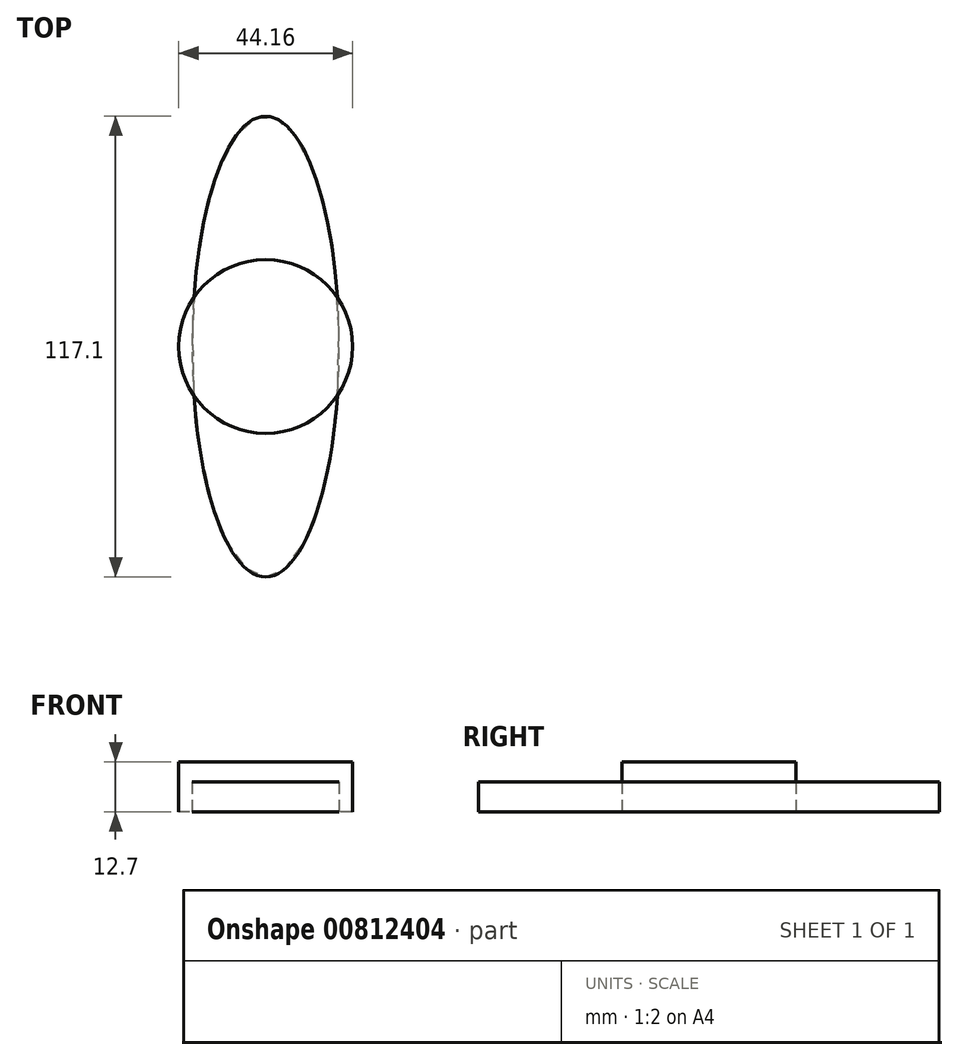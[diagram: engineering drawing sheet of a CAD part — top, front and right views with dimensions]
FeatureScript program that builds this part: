
annotation { "Feature Type Name" : "Feature", "Feature Type Description" : "" }
export const myFeature = defineFeature(function(context is Context, id is Id, definition is map)
    precondition{}
    {
        {
            var Q0;
            Q0=qCreatedBy(makeId("Top.planeOp"),FACE);
            var sketch = newSketch(context, id + "F0", { "sketchPlane" : qUnion([Q0])});
            skCircle(sketch, "E0", {"center": v(0, 0) * mm, "radius": 22.08 * mm});
            skSolve(sketch);
        }
        {
            var Q0;
            Q0 = qSketchRegion(id + "F0", true);
            extrude(context, id + "F1", {"entities" : qUnion([Q0]), "depth" : 12.7 * mm, "offsetDistance" : 25.4 * mm});
        }
        {
            var Q0;
            Q0=qCreatedBy(makeId("Top.planeOp"),FACE);
            var sketch = newSketch(context, id + "F2", { "sketchPlane" : qUnion([Q0])});
            skEllipse(sketch, "E1", {"center": v(0, 0) * mm, "majorRadius": 59.16 * mm, "minorRadius": 17.85 * mm, "majorAxis": v(1, 0)});
            skSolve(sketch);
        }
        {
            var Q0;
            Q0=makeQuery(id+"F2.imprint","IMPRINT",FACE,{"disambiguationData":[TD([[makeQuery(id+"F2.imprint","IMPRINT",EDGE,{"derivedFrom":sQuery(id+"F2.wireOp",EDGE,"E1")}),1.0]])]});
            extrude(context, id + "F3", {"entities" : qUnion([Q0]), "depth" : 7.62 * mm, "offsetDistance" : 25.4 * mm});
        }
        {
            var Q0;
            Q0=qCreatedBy(makeId("Top.planeOp"),FACE);
            var sketch = newSketch(context, id + "F4", { "sketchPlane" : qUnion([Q0])});
            skEllipse(sketch, "E2", {"center": v(0, 0) * mm, "majorRadius": 58.55 * mm, "minorRadius": 18.68 * mm, "majorAxis": v(0, -1)});
            skSolve(sketch);
        }
        {
            var Q0;
            Q0=makeQuery(id+"F4.imprint","IMPRINT",FACE,{"disambiguationData":[TD([[makeQuery(id+"F4.imprint","IMPRINT",EDGE,{"derivedFrom":sQuery(id+"F4.wireOp",EDGE,"E2")}),1.0]])]});
            extrude(context, id + "F5", {"entities" : qUnion([Q0]), "depth" : 7.62 * mm, "offsetDistance" : 25.4 * mm});
        }
        {
            var Q0;
            Q0=makeQuery(id+"F3.opExtrude","SWEPT_BODY",BODY,{"disambiguationData":[OSD([sQuery(id+"F2.wireOp",EDGE,"E1")])]});
            deleteBodies(context, id + "F6", {"entities" : qUnion([Q0])});
        }
    });
